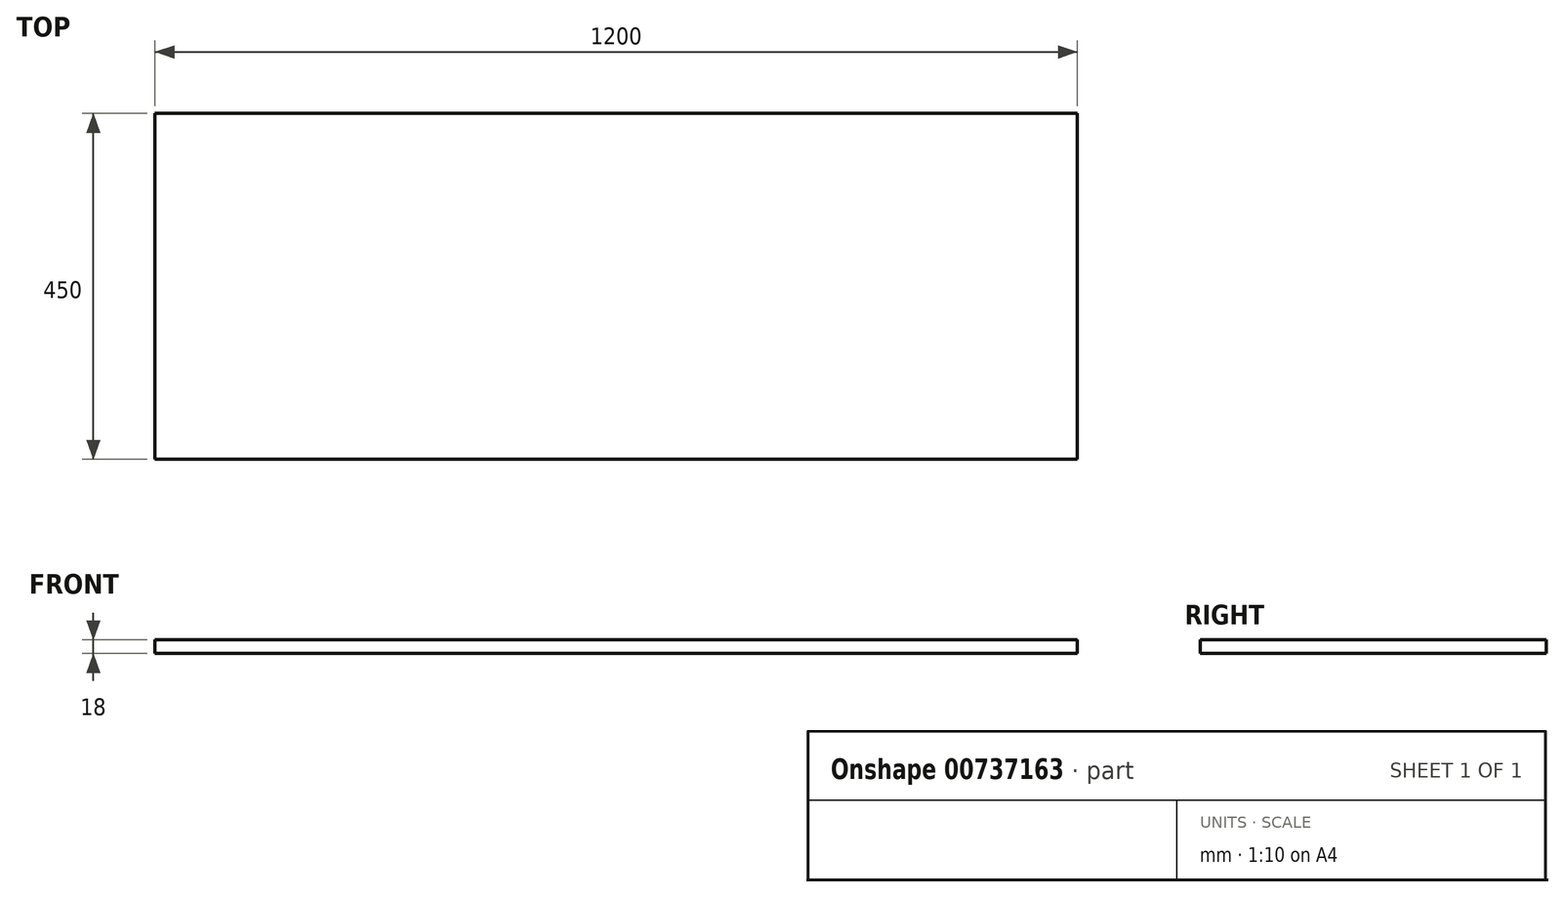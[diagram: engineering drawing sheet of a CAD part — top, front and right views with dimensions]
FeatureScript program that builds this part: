
annotation { "Feature Type Name" : "Feature", "Feature Type Description" : "" }
export const myFeature = defineFeature(function(context is Context, id is Id, definition is map)
    precondition{}
    {
        {
            var Q0;
            Q0=qCreatedBy(makeId("Front.planeOp"),FACE);
            var sketch = newSketch(context, id + "F0", { "sketchPlane" : qUnion([Q0])});
            skLineSegment(sketch, "E0.bottom", {"start": v(600, 9) * mm, "end": v(-600, 9) * mm});
            skLineSegment(sketch, "E0.top", {"start": v(600, -9) * mm, "end": v(-600, -9) * mm});
            skLineSegment(sketch, "E0.left", {"start": v(600, 9) * mm, "end": v(600, -9) * mm});
            skLineSegment(sketch, "E0.right", {"start": v(-600, 9) * mm, "end": v(-600, -9) * mm});
            skPoint(sketch, "E0.middle", {"position": v(0, 0) * mm});
            skSolve(sketch);
        }
        {
            var Q0;
            Q0 = qSketchRegion(id + "F0", true);
            extrude(context, id + "F1", {"entities" : qUnion([Q0]), "endBound" : BoundingType.SYMMETRIC, "depth" : 450 * mm, "offsetDistance" : 25 * mm});
        }
    });
